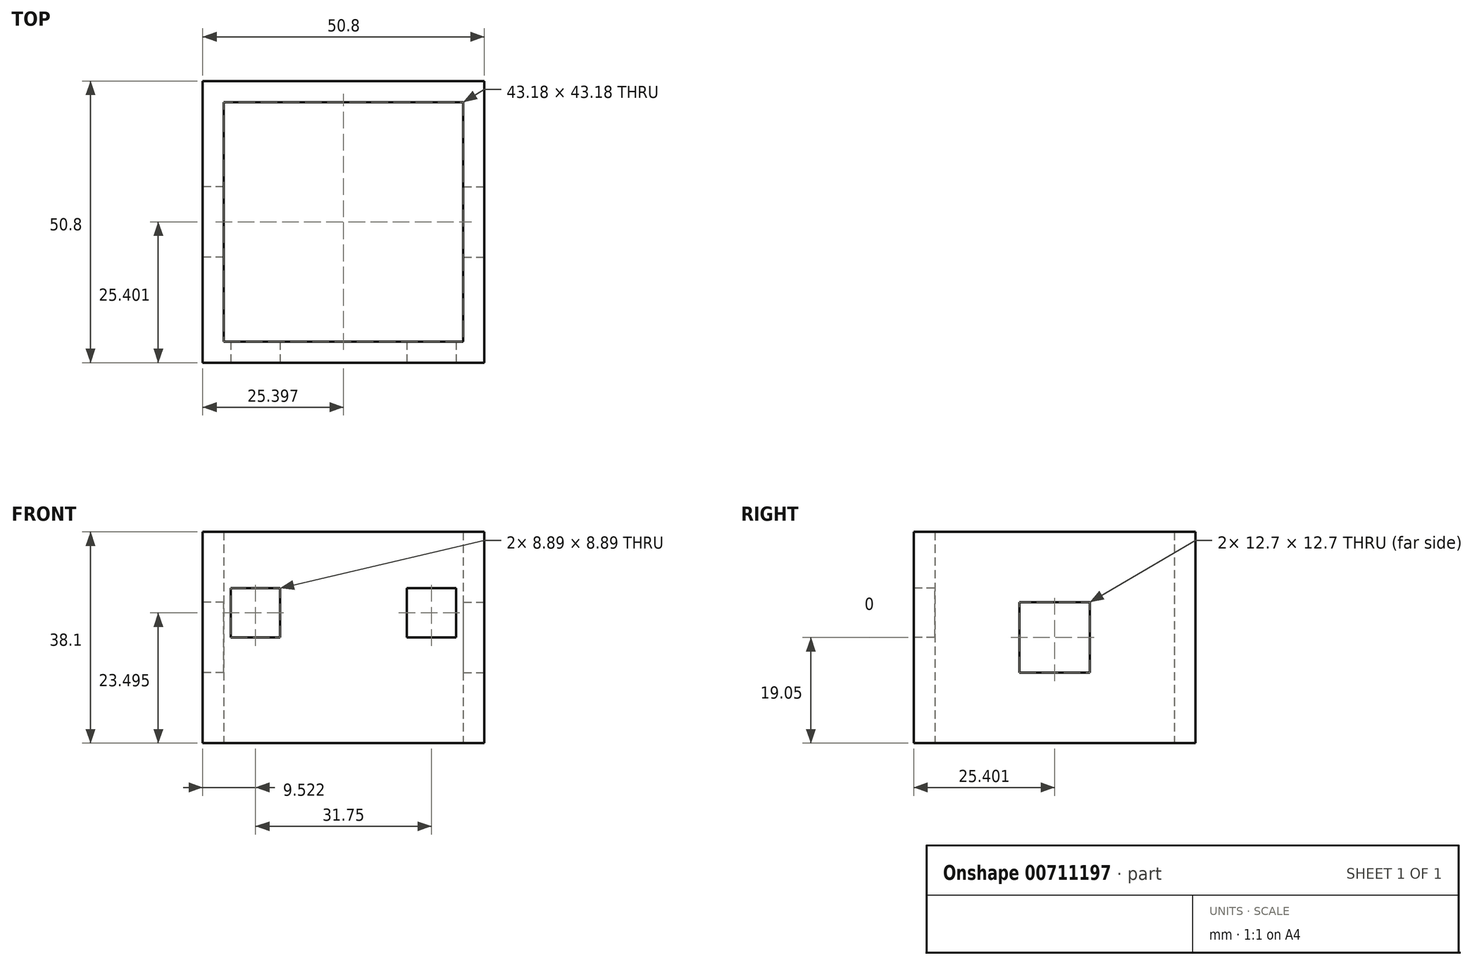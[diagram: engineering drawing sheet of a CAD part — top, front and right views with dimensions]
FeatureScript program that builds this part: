
annotation { "Feature Type Name" : "Feature", "Feature Type Description" : "" }
export const myFeature = defineFeature(function(context is Context, id is Id, definition is map)
    precondition{}
    {
        {
            var Q0;
            Q0=qCreatedBy(makeId("Top.planeOp"),FACE);
            var sketch = newSketch(context, id + "F0", { "sketchPlane" : qUnion([Q0])});
            skLineSegment(sketch, "E0.bottom", {"start": v(-25.27, 23.7) * mm, "end": v(25.53, 23.7) * mm});
            skLineSegment(sketch, "E0.top", {"start": v(-25.27, -27.1) * mm, "end": v(25.53, -27.1) * mm});
            skLineSegment(sketch, "E0.left", {"start": v(-25.27, 23.7) * mm, "end": v(-25.27, -27.1) * mm});
            skLineSegment(sketch, "E0.right", {"start": v(25.53, 23.7) * mm, "end": v(25.53, -27.1) * mm});
            skSolve(sketch);
        }
        {
            var Q0;
            Q0 = qSketchRegion(id + "F0", true);
            extrude(context, id + "F1", {"entities" : qUnion([Q0]), "depth" : 38.1 * mm, "offsetDistance" : 25.4 * mm});
        }
        {
            var Q0;
            Q0=makeQuery(id+"F1.opExtrude","CAP_FACE",FACE,{"disambiguationData":[OSD([sQuery(id+"F0.wireOp",EDGE,"E0.bottom"),sQuery(id+"F0.wireOp",EDGE,"E0.top"),sQuery(id+"F0.wireOp",EDGE,"E0.left"),sQuery(id+"F0.wireOp",EDGE,"E0.right")])],"isStart":false});
            var Q1;
            Q1=makeQuery(id+"F1.opExtrude","CAP_FACE",FACE,{"disambiguationData":[OSD([sQuery(id+"F0.wireOp",EDGE,"E0.bottom"),sQuery(id+"F0.wireOp",EDGE,"E0.top"),sQuery(id+"F0.wireOp",EDGE,"E0.left"),sQuery(id+"F0.wireOp",EDGE,"E0.right")])],"isStart":true});
            shell(context, id + "F2", {"entities" : qUnion([Q0, Q1]), "thickness" : 3.8 * mm});
        }
        {
            var Q0;
            Q0=makeQuery(id+"F1.opExtrude","SWEPT_FACE",FACE,{"disambiguationData":[OSD([sQuery(id+"F0.wireOp",EDGE,"E0.top")])]});
            var sketch = newSketch(context, id + "F3", { "sketchPlane" : qUnion([Q0])});
            skFitSpline(sketch, "E1", {"points": [v(-6.96, 1.27) * mm, v(-6.96, 3.83) * mm, v(-6.96, 12.05) * mm, v(-6.96, 19.81) * mm, v(-6.96, 25.22) * mm, v(-6.96, 25.8) * mm, v(-6.96, 25.9) * mm, v(-6.82, 25.9) * mm, v(-5.98, 25.9) * mm, v(-5.16, 25.9) * mm, v(-2.68, 25.9) * mm, v(1.32, 25.9) * mm, v(5.14, 25.9) * mm, v(6.83, 25.9) * mm, v(7.05, 25.9) * mm, v(7.05, 25.87) * mm, v(7.05, 19.3) * mm, v(7.05, 11.73) * mm, v(7.05, 8.02) * mm, v(7.05, 5) * mm, v(7.05, 1.4) * mm, v(7.05, 1.27) * mm, v(6.7, 1.27) * mm, v(-2.98, 1.27) * mm, v(-6.6, 1.27) * mm, v(-6.93, 1.27) * mm, v(-6.96, 1.27) * mm]});
            skFitSpline(sketch, "E2", {"points": [v(-1.72, 18.69) * mm, v(-1.71, 19.1) * mm, v(-1.45, 19.55) * mm, v(-1.05, 19.92) * mm, v(-0.8, 20.05) * mm, v(-0.41, 20.09) * mm, v(0, 20.08) * mm, v(0.49, 19.75) * mm, v(0.87, 19.4) * mm, v(0.97, 19.2) * mm, v(1.06, 18.94) * mm, v(1.09, 18.71) * mm, v(0.87, 18.69) * mm, v(-0.52, 18.7) * mm, v(-1.39, 18.7) * mm, v(-1.62, 18.7) * mm, v(-1.72, 18.69) * mm]});
            skFitSpline(sketch, "E3", {"points": [v(-1.58, 19.39) * mm, v(-4.76, 19.75) * mm, v(-4.85, 19.76) * mm, v(-4.85, 19.88) * mm, v(-4.51, 20.74) * mm, v(-4.1, 21.42) * mm, v(-3.62, 22) * mm, v(-3.44, 22.18) * mm, v(-3.4, 22.15) * mm, v(-1.3, 20.05) * mm, v(-1.1, 19.87) * mm, v(-1.16, 19.83) * mm, v(-1.4, 19.6) * mm, v(-1.51, 19.47) * mm, v(-1.58, 19.39) * mm]});
            skFitSpline(sketch, "E4", {"points": [v(-1.67, 19.2) * mm, v(-1.82, 19.22) * mm, v(-2, 19.23) * mm, v(-2.13, 19.24) * mm, v(-4.9, 19.6) * mm, v(-4.9, 19.6) * mm, v(-4.93, 18.79) * mm, v(-4.88, 18.79) * mm, v(-4.85, 18.79) * mm, v(-1.84, 18.78) * mm, v(-1.75, 18.78) * mm, v(-1.73, 19) * mm, v(-1.71, 19.1) * mm, v(-1.67, 19.2) * mm]});
            skFitSpline(sketch, "E5", {"points": [v(-0.36, 20.1) * mm, v(-0.36, 21.35) * mm, v(-0.36, 22.34) * mm, v(-0.36, 23.4) * mm, v(-0.37, 23.44) * mm, v(-0.93, 23.42) * mm, v(-1.55, 23.28) * mm, v(-2.12, 23.05) * mm, v(-2.48, 22.88) * mm, v(-2.97, 22.58) * mm, v(-3.26, 22.34) * mm, v(-3.25, 22.3) * mm, v(-3, 22.07) * mm, v(-2.36, 21.44) * mm, v(-1.67, 20.72) * mm, v(-1.2, 20.23) * mm, v(-1, 20) * mm, v(-0.97, 19.98) * mm, v(-0.86, 20.03) * mm, v(-0.52, 20.08) * mm, v(-0.41, 20.09) * mm, v(-0.36, 20.1) * mm]});
            skFitSpline(sketch, "E6", {"points": [v(-0.16, 20.1) * mm, v(-0.16, 20.2) * mm, v(-0.15, 22.34) * mm, v(-0.16, 23.39) * mm, v(-0.14, 23.44) * mm, v(0.4, 23.42) * mm, v(1, 23.29) * mm, v(1.52, 23.12) * mm, v(2.13, 22.8) * mm, v(2.58, 22.5) * mm, v(2.69, 22.4) * mm, v(2.71, 22.38) * mm, v(2.68, 22.33) * mm, v(2.18, 21.84) * mm, v(1.61, 21.27) * mm, v(1, 20.67) * mm, v(0.7, 20.33) * mm, v(0.37, 19.98) * mm, v(0.28, 19.92) * mm, v(0.25, 19.95) * mm, v(0.05, 20.07) * mm, v(-0.16, 20.1) * mm]});
            skFitSpline(sketch, "E7", {"points": [v(0.4, 19.82) * mm, v(1.52, 20.89) * mm, v(2.13, 21.5) * mm, v(2.55, 21.93) * mm, v(2.83, 22.2) * mm, v(2.87, 22.24) * mm, v(2.95, 22.2) * mm, v(3.32, 21.82) * mm, v(3.73, 21.27) * mm, v(4, 20.77) * mm, v(4.22, 20.26) * mm, v(4.33, 19.88) * mm, v(4.34, 19.75) * mm, v(4.2, 19.75) * mm, v(4.12, 19.75) * mm, v(3.82, 19.75) * mm, v(2.66, 19.63) * mm, v(1.72, 19.5) * mm, v(1, 19.38) * mm, v(0.9, 19.36) * mm, v(0.87, 19.4) * mm, v(0.73, 19.55) * mm, v(0.6, 19.65) * mm, v(0.49, 19.75) * mm, v(0.4, 19.82) * mm]});
            skFitSpline(sketch, "E8", {"points": [v(0.97, 19.2) * mm, v(1.66, 19.3) * mm, v(2.67, 19.4) * mm, v(3.46, 19.5) * mm, v(4.03, 19.57) * mm, v(4.27, 19.59) * mm, v(4.35, 19.6) * mm, v(4.4, 19.54) * mm, v(4.45, 19.3) * mm, v(4.47, 18.96) * mm, v(4.47, 18.75) * mm, v(4.45, 18.73) * mm, v(4.4, 18.73) * mm, v(3.2, 18.73) * mm, v(2.62, 18.74) * mm, v(2.08, 18.74) * mm, v(1.46, 18.74) * mm, v(1.15, 18.74) * mm, v(1.1, 18.78) * mm, v(1.09, 18.84) * mm, v(1.06, 18.94) * mm, v(1, 19.1) * mm, v(0.99, 19.16) * mm, v(0.97, 19.2) * mm]});
            skFitSpline(sketch, "E9", {"points": [v(-5.01, 17.01) * mm, v(-5, 16.91) * mm, v(-5.02, 13.55) * mm, v(-5.01, 10.44) * mm, v(-5, 10.3) * mm, v(-4.5, 10.3) * mm, v(-3.1, 10.29) * mm, v(-1.25, 10.26) * mm, v(-1.12, 10.26) * mm, v(-1.13, 10.37) * mm, v(-1.13, 13.61) * mm, v(-1.12, 16.87) * mm, v(-1.12, 16.98) * mm, v(-1.24, 17) * mm, v(-4.88, 17.01) * mm, v(-5.01, 17.01) * mm]});
            skFitSpline(sketch, "E10", {"points": [v(0.67, 17) * mm, v(0.65, 16.85) * mm, v(0.68, 13.6) * mm, v(0.68, 10.33) * mm, v(0.68, 10.3) * mm, v(0.7, 10.3) * mm, v(0.77, 10.3) * mm, v(4.35, 10.3) * mm, v(4.46, 10.3) * mm, v(4.53, 10.3) * mm, v(4.54, 10.31) * mm, v(4.54, 10.35) * mm, v(4.55, 13.6) * mm, v(4.54, 16.9) * mm, v(4.54, 16.98) * mm, v(4.54, 17) * mm, v(4.39, 17) * mm, v(1.88, 17) * mm, v(0.75, 17) * mm, v(0.67, 17) * mm]});
            skFitSpline(sketch, "E11", {"points": [v(-5.03, 8.77) * mm, v(-5.03, 8.74) * mm, v(-5.01, 5.7) * mm, v(-5.03, 2.07) * mm, v(-5.03, 2.03) * mm, v(-4.97, 2.03) * mm, v(-1.2, 2.02) * mm, v(-1.14, 2.02) * mm, v(-1.12, 2.02) * mm, v(-1.12, 2.12) * mm, v(-1.13, 2.63) * mm, v(-1.15, 5.73) * mm, v(-1.14, 8.68) * mm, v(-1.14, 8.75) * mm, v(-1.15, 8.76) * mm, v(-1.24, 8.76) * mm, v(-4.87, 8.77) * mm, v(-4.97, 8.77) * mm, v(-5.03, 8.77) * mm]});
            skFitSpline(sketch, "E12", {"points": [v(0.66, 8.77) * mm, v(0.66, 8.73) * mm, v(0.67, 5.7) * mm, v(0.67, 2.13) * mm, v(0.66, 2.06) * mm, v(0.67, 2.03) * mm, v(0.72, 2.02) * mm, v(4.48, 2.03) * mm, v(4.54, 2.03) * mm, v(4.56, 2.06) * mm, v(4.57, 2.14) * mm, v(4.57, 5.56) * mm, v(4.56, 8.7) * mm, v(4.57, 8.74) * mm, v(4.52, 8.75) * mm, v(0.75, 8.76) * mm, v(0.66, 8.77) * mm]});
            skFitSpline(sketch, "E13", {"points": [v(5.27, 13.7) * mm, v(5.36, 13.7) * mm, v(5.6, 13.7) * mm, v(6.9, 13.68) * mm, v(6.92, 13.68) * mm, v(6.92, 13.63) * mm, v(6.91, 11.48) * mm, v(6.92, 11.37) * mm, v(6.92, 11.3) * mm, v(6.89, 11.34) * mm, v(6.62, 11.62) * mm, v(6.4, 11.77) * mm, v(6.12, 11.8) * mm, v(5.81, 11.76) * mm, v(5.57, 11.64) * mm, v(5.36, 11.45) * mm, v(5.26, 11.32) * mm, v(5.26, 11.4) * mm, v(5.27, 13.52) * mm, v(5.27, 13.65) * mm, v(5.27, 13.7) * mm]});
            skFitSpline(sketch, "E14", {"points": [v(6.92, 11.3) * mm, v(6.98, 11.16) * mm, v(7.02, 10.95) * mm, v(7.02, 10.7) * mm, v(6.96, 10.46) * mm, v(6.77, 10.17) * mm, v(6.5, 9.96) * mm, v(6.17, 9.91) * mm, v(5.85, 9.91) * mm, v(5.6, 10.04) * mm, v(5.37, 10.24) * mm, v(5.17, 10.54) * mm, v(5.14, 11.02) * mm, v(5.22, 11.26) * mm, v(5.26, 11.32) * mm, v(5.36, 11.45) * mm, v(5.57, 11.64) * mm, v(5.81, 11.76) * mm, v(6.12, 11.8) * mm, v(6.4, 11.77) * mm, v(6.62, 11.62) * mm, v(6.89, 11.34) * mm, v(6.92, 11.3) * mm]});
            skFitSpline(sketch, "E15", {"points": [v(5.25, 10.38) * mm, v(5.25, 10.34) * mm, v(5.26, 9.42) * mm, v(5.26, 9.37) * mm, v(5.26, 9.36) * mm, v(5.27, 9.36) * mm, v(5.4, 9.36) * mm, v(6.83, 9.37) * mm, v(6.88, 9.37) * mm, v(6.92, 9.37) * mm, v(6.92, 9.4) * mm, v(6.92, 10.3) * mm, v(6.92, 10.36) * mm, v(6.92, 10.39) * mm, v(6.9, 10.35) * mm, v(6.77, 10.17) * mm, v(6.5, 9.96) * mm, v(6.17, 9.91) * mm, v(5.85, 9.91) * mm, v(5.6, 10.04) * mm, v(5.37, 10.24) * mm, v(5.25, 10.38) * mm]});
            skSolve(sketch);
        }
        {
            var Q0;
            Q0=sQuery(id+"F3.wireOp",EDGE,"E4");
            extrude(context, id + "F4", {"bodyType" : ToolBodyType.SURFACE, "surfaceEntities" : qUnion([Q0]), "depth" : -0.25 * mm, "offsetDistance" : 25.4 * mm});
        }
        {
            var Q0;
            {var subQ0=sQuery(id+"F3.wireOp",EDGE,"E3");var subQ1=sQuery(id+"F3.wireOp",EDGE,"E2");var subQ4=makeQuery(id+"F3.imprint","INTERSECT",VERTEX,{"disambiguationData":[OD(0.0)],"derivedFrom":[subQ1,subQ0]});Q0=makeQuery(id+"F3.imprint","IMPRINT",FACE,{"disambiguationData":[TD([[makeQuery(id+"F3.imprint","IMPRINT",EDGE,{"disambiguationData":[TD([[subQ4,-1.0]])],"derivedFrom":subQ1}),1.0]])]});}
            var Q1;
            {var subQ0=sQuery(id+"F3.wireOp",EDGE,"E5");var subQ1=sQuery(id+"F3.wireOp",EDGE,"E2");var subQ7=makeQuery(id+"F3.imprint","INTERSECT",VERTEX,{"disambiguationData":[OD(0.0)],"derivedFrom":[subQ1,subQ0]});Q1=makeQuery(id+"F3.imprint","IMPRINT",FACE,{"disambiguationData":[TD([[makeQuery(id+"F3.imprint","IMPRINT",EDGE,{"disambiguationData":[TD([[subQ7,1.0]])],"derivedFrom":subQ1}),1.0]])]});}
            var Q2;
            {var subQ0=sQuery(id+"F3.wireOp",EDGE,"E6");var subQ1=sQuery(id+"F3.wireOp",EDGE,"E2");var subQ2=makeQuery(id+"F3.imprint","INTERSECT",VERTEX,{"disambiguationData":[OD(0.0)],"derivedFrom":[subQ1,subQ0]});Q2=makeQuery(id+"F3.imprint","IMPRINT",FACE,{"disambiguationData":[TD([[makeQuery(id+"F3.imprint","IMPRINT",EDGE,{"disambiguationData":[TD([[subQ2,-1.0]])],"derivedFrom":subQ1}),1.0]])]});}
            var Q3;
            {var subQ0=sQuery(id+"F3.wireOp",EDGE,"E7");var subQ1=sQuery(id+"F3.wireOp",EDGE,"E2");var subQ4=makeQuery(id+"F3.imprint","INTERSECT",VERTEX,{"disambiguationData":[OD(0.0)],"derivedFrom":[subQ1,subQ0]});Q3=makeQuery(id+"F3.imprint","IMPRINT",FACE,{"disambiguationData":[TD([[makeQuery(id+"F3.imprint","IMPRINT",EDGE,{"disambiguationData":[TD([[subQ4,-1.0]])],"derivedFrom":subQ1}),1.0]])]});}
            var Q4;
            {var subQ0=sQuery(id+"F3.wireOp",EDGE,"E8");var subQ1=sQuery(id+"F3.wireOp",EDGE,"E2");var subQ4=makeQuery(id+"F3.imprint","INTERSECT",VERTEX,{"disambiguationData":[OD(0.0)],"derivedFrom":[subQ1,subQ0]});Q4=makeQuery(id+"F3.imprint","IMPRINT",FACE,{"disambiguationData":[TD([[makeQuery(id+"F3.imprint","IMPRINT",EDGE,{"disambiguationData":[TD([[subQ4,-1.0]])],"derivedFrom":subQ1}),1.0]])]});}
            var Q5;
            Q5=makeQuery(id+"F3.imprint","IMPRINT",FACE,{"disambiguationData":[TD([[makeQuery(id+"F3.imprint","IMPRINT",EDGE,{"derivedFrom":sQuery(id+"F3.wireOp",EDGE,"E9")}),1.0]])]});
            var Q6;
            Q6=makeQuery(id+"F3.imprint","IMPRINT",FACE,{"disambiguationData":[TD([[makeQuery(id+"F3.imprint","IMPRINT",EDGE,{"derivedFrom":sQuery(id+"F3.wireOp",EDGE,"E10")}),1.0]])]});
            var Q7;
            Q7=makeQuery(id+"F3.imprint","IMPRINT",FACE,{"disambiguationData":[TD([[makeQuery(id+"F3.imprint","IMPRINT",EDGE,{"derivedFrom":sQuery(id+"F3.wireOp",EDGE,"E11")}),1.0]])]});
            var Q8;
            Q8=makeQuery(id+"F3.imprint","IMPRINT",FACE,{"disambiguationData":[TD([[makeQuery(id+"F3.imprint","IMPRINT",EDGE,{"derivedFrom":sQuery(id+"F3.wireOp",EDGE,"E12")}),1.0]])]});
            var Q9;
            Q9=sQuery(id+"F3.wireOp",EDGE,"E3");
            var Q10;
            Q10=sQuery(id+"F3.wireOp",EDGE,"E5");
            var Q11;
            Q11=sQuery(id+"F3.wireOp",EDGE,"E6");
            var Q12;
            Q12=sQuery(id+"F3.wireOp",EDGE,"E7");
            var Q13;
            Q13=sQuery(id+"F3.wireOp",EDGE,"E8");
            var Q14;
            Q14=sQuery(id+"F3.wireOp",EDGE,"E10");
            var Q15;
            Q15=sQuery(id+"F3.wireOp",EDGE,"E9");
            var Q16;
            Q16=sQuery(id+"F3.wireOp",EDGE,"E11");
            var Q17;
            Q17=sQuery(id+"F3.wireOp",EDGE,"E12");
            extrude(context, id + "F5", {"entities" : qUnion([Q0, Q1, Q2, Q3, Q4, Q5, Q6, Q7, Q8]), "bodyType" : ToolBodyType.SURFACE, "operationType" : NewBodyOperationType.ADD, "surfaceEntities" : qUnion([Q9, Q10, Q11, Q12, Q13, Q14, Q15, Q16, Q17]), "depth" : -0.25 * mm, "offsetDistance" : 25.4 * mm});
        }
        {
            var Q0;
            {var subQ0=sQuery(id+"F3.wireOp",EDGE,"E14");var subQ1=sQuery(id+"F3.wireOp",EDGE,"E13");var subQ9=makeQuery(id+"F3.imprint","INTERSECT",VERTEX,{"disambiguationData":[OD(2.0)],"derivedFrom":[subQ1,subQ0]});Q0=makeQuery(id+"F3.imprint","IMPRINT",FACE,{"disambiguationData":[TD([[makeQuery(id+"F3.imprint","IMPRINT",EDGE,{"disambiguationData":[TD([[subQ9,1.0]])],"derivedFrom":subQ1}),1.0]])]});}
            var Q1;
            Q1=sQuery(id+"F3.wireOp",EDGE,"E14");
            extrude(context, id + "F6", {"entities" : qUnion([Q0]), "bodyType" : ToolBodyType.SURFACE, "operationType" : NewBodyOperationType.ADD, "surfaceEntities" : qUnion([Q1]), "depth" : 0.25 * mm, "offsetDistance" : 25.4 * mm});
        }
        {
            var Q0;
            {var subQ0=sQuery(id+"F3.wireOp",EDGE,"E14");var subQ1=sQuery(id+"F3.wireOp",EDGE,"E13");var subQ8=makeQuery(id+"F3.imprint","INTERSECT",VERTEX,{"disambiguationData":[OD(2.0)],"derivedFrom":[subQ1,subQ0]});Q0=makeQuery(id+"F3.imprint","IMPRINT",FACE,{"disambiguationData":[TD([[makeQuery(id+"F3.imprint","IMPRINT",EDGE,{"disambiguationData":[TD([[subQ8,-1.0]])],"derivedFrom":subQ1}),-1.0]])]});}
            var Q1;
            {var subQ0=sQuery(id+"F3.wireOp",EDGE,"E15");var subQ1=sQuery(id+"F3.wireOp",EDGE,"E14");var subQ8=makeQuery(id+"F3.imprint","INTERSECT",VERTEX,{"disambiguationData":[OD(2.0)],"derivedFrom":[subQ1,subQ0]});Q1=makeQuery(id+"F3.imprint","IMPRINT",FACE,{"disambiguationData":[TD([[makeQuery(id+"F3.imprint","IMPRINT",EDGE,{"disambiguationData":[TD([[subQ8,-1.0]])],"derivedFrom":subQ1}),1.0]])]});}
            var Q2;
            Q2=sQuery(id+"F3.wireOp",EDGE,"E13");
            var Q3;
            Q3=sQuery(id+"F3.wireOp",EDGE,"E15");
            extrude(context, id + "F7", {"entities" : qUnion([Q0, Q1]), "bodyType" : ToolBodyType.SURFACE, "operationType" : NewBodyOperationType.ADD, "surfaceEntities" : qUnion([Q2, Q3]), "depth" : 0.25 * mm, "offsetDistance" : 25.4 * mm});
        }
        {
            var Q0;
            {var subQ1=sQuery(id+"F3.wireOp",EDGE,"E2");var subQ4=sQuery(id+"F3.wireOp",EDGE,"E4");var subQ7=makeQuery(id+"F3.imprint","INTERSECT",VERTEX,{"disambiguationData":[OD(0.0)],"derivedFrom":[subQ1,subQ4]});Q0=makeQuery(id+"F3.imprint","IMPRINT",FACE,{"disambiguationData":[TD([[makeQuery(id+"F3.imprint","IMPRINT",EDGE,{"disambiguationData":[TD([[subQ7,-1.0]])],"derivedFrom":subQ1}),-1.0]])]});}
            var Q1;
            Q1=sQuery(id+"F3.wireOp",EDGE,"E2");
            extrude(context, id + "F8", {"entities" : qUnion([Q0]), "bodyType" : ToolBodyType.SURFACE, "surfaceEntities" : qUnion([Q1]), "depth" : 0.25 * mm, "offsetDistance" : 25.4 * mm});
        }
        {
            var Q0;
            Q0=makeQuery(id+"F3.imprint","IMPRINT",FACE,{"disambiguationData":[TD([[makeQuery(id+"F3.imprint","IMPRINT",EDGE,{"derivedFrom":sQuery(id+"F3.wireOp",EDGE,"E1")}),-1.0]])]});
            var Q1;
            Q1=sQuery(id+"F3.wireOp",EDGE,"E1");
            extrude(context, id + "F9", {"entities" : qUnion([Q0]), "bodyType" : ToolBodyType.SURFACE, "surfaceEntities" : qUnion([Q1]), "endBound" : BoundingType.SYMMETRIC, "depth" : 0.25 * mm, "offsetDistance" : 25.4 * mm});
        }
        {
            var Q0;
            Q0=makeQuery(id+"F1.opExtrude","SWEPT_FACE",FACE,{"disambiguationData":[OSD([sQuery(id+"F0.wireOp",EDGE,"E0.right")])]});
            var sketch = newSketch(context, id + "F10", { "sketchPlane" : qUnion([Q0])});
            skLineSegment(sketch, "E16.bottom", {"start": v(-8.05, 25.4) * mm, "end": v(4.65, 25.4) * mm});
            skLineSegment(sketch, "E16.top", {"start": v(-8.05, 12.7) * mm, "end": v(4.65, 12.7) * mm});
            skLineSegment(sketch, "E16.left", {"start": v(-8.05, 25.4) * mm, "end": v(-8.05, 12.7) * mm});
            skLineSegment(sketch, "E16.right", {"start": v(4.65, 25.4) * mm, "end": v(4.65, 12.7) * mm});
            skSolve(sketch);
        }
        {
            var Q0;
            Q0=makeQuery(id+"F10.imprint","IMPRINT",FACE,{"disambiguationData":[TD([[makeQuery(id+"F10.imprint","IMPRINT",EDGE,{"derivedFrom":sQuery(id+"F10.wireOp",EDGE,"E16.bottom")}),-1.0]])]});
            extrude(context, id + "F11", {"entities" : qUnion([Q0]), "operationType" : NewBodyOperationType.REMOVE, "oppositeDirection" : true, "depth" : 25.4 * mm, "offsetDistance" : 25.4 * mm});
        }
        {
            var Q0;
            Q0=makeQuery(id+"F1.opExtrude","SWEPT_FACE",FACE,{"disambiguationData":[OSD([sQuery(id+"F0.wireOp",EDGE,"E0.left")])]});
            var sketch = newSketch(context, id + "F12", { "sketchPlane" : qUnion([Q0])});
            skLineSegment(sketch, "E17.bottom", {"start": v(-4.65, 25.4) * mm, "end": v(8.05, 25.4) * mm});
            skLineSegment(sketch, "E17.top", {"start": v(-4.65, 12.7) * mm, "end": v(8.05, 12.7) * mm});
            skLineSegment(sketch, "E17.left", {"start": v(-4.65, 25.4) * mm, "end": v(-4.65, 12.7) * mm});
            skLineSegment(sketch, "E17.right", {"start": v(8.05, 25.4) * mm, "end": v(8.05, 12.7) * mm});
            skSolve(sketch);
        }
        {
            var Q0;
            Q0=makeQuery(id+"F12.imprint","IMPRINT",FACE,{"disambiguationData":[TD([[makeQuery(id+"F12.imprint","IMPRINT",EDGE,{"derivedFrom":sQuery(id+"F12.wireOp",EDGE,"E17.bottom")}),-1.0]])]});
            extrude(context, id + "F13", {"entities" : qUnion([Q0]), "operationType" : NewBodyOperationType.REMOVE, "oppositeDirection" : true, "depth" : 25.4 * mm, "offsetDistance" : 25.4 * mm});
        }
        {
            var Q0;
            Q0=makeQuery(id+"F1.opExtrude","SWEPT_FACE",FACE,{"disambiguationData":[OSD([sQuery(id+"F0.wireOp",EDGE,"E0.top")])]});
            var sketch = newSketch(context, id + "F14", { "sketchPlane" : qUnion([Q0])});
            skLineSegment(sketch, "E18.bottom", {"start": v(-20.2, 27.94) * mm, "end": v(-11.3, 27.94) * mm});
            skLineSegment(sketch, "E18.top", {"start": v(-20.2, 19.05) * mm, "end": v(-11.3, 19.05) * mm});
            skLineSegment(sketch, "E18.left", {"start": v(-20.2, 27.94) * mm, "end": v(-20.2, 19.05) * mm});
            skLineSegment(sketch, "E18.right", {"start": v(-11.3, 27.94) * mm, "end": v(-11.3, 19.05) * mm});
            skLineSegment(sketch, "E19.bottom", {"start": v(11.56, 27.94) * mm, "end": v(20.45, 27.94) * mm});
            skLineSegment(sketch, "E19.top", {"start": v(11.56, 19.05) * mm, "end": v(20.45, 19.05) * mm});
            skLineSegment(sketch, "E19.left", {"start": v(11.56, 27.94) * mm, "end": v(11.56, 19.05) * mm});
            skLineSegment(sketch, "E19.right", {"start": v(20.45, 27.94) * mm, "end": v(20.45, 19.05) * mm});
            skSolve(sketch);
        }
        {
            var Q0;
            Q0=makeQuery(id+"F14.imprint","IMPRINT",FACE,{"disambiguationData":[TD([[makeQuery(id+"F14.imprint","IMPRINT",EDGE,{"derivedFrom":sQuery(id+"F14.wireOp",EDGE,"E19.bottom")}),-1.0]])]});
            var Q1;
            Q1=makeQuery(id+"F14.imprint","IMPRINT",FACE,{"disambiguationData":[TD([[makeQuery(id+"F14.imprint","IMPRINT",EDGE,{"derivedFrom":sQuery(id+"F14.wireOp",EDGE,"E18.bottom")}),-1.0]])]});
            extrude(context, id + "F15", {"entities" : qUnion([Q0, Q1]), "operationType" : NewBodyOperationType.REMOVE, "oppositeDirection" : true, "depth" : 25.4 * mm, "offsetDistance" : 25.4 * mm});
        }
    });
